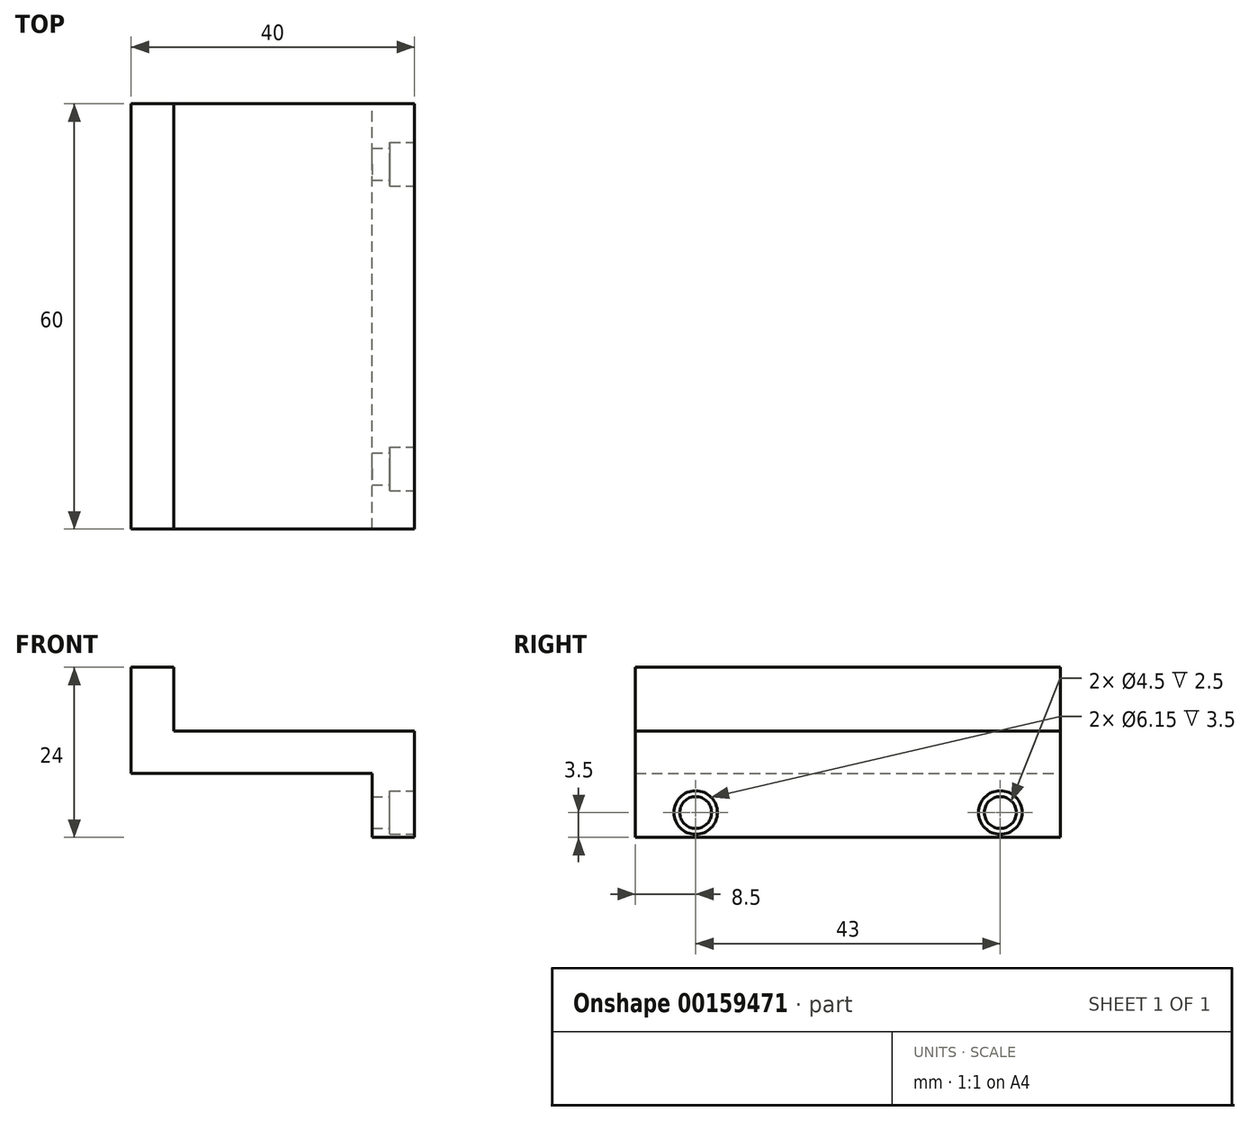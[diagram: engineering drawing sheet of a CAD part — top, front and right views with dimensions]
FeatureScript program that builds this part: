
annotation { "Feature Type Name" : "Feature", "Feature Type Description" : "" }
export const myFeature = defineFeature(function(context is Context, id is Id, definition is map)
    precondition{}
    {
        {
            var Q0;
            Q0=qCreatedBy(makeId("Top.planeOp"),FACE);
            var sketch = newSketch(context, id + "F0", { "sketchPlane" : qUnion([Q0])});
            skLineSegment(sketch, "E0.bottom", {"start": v(20, 30) * mm, "end": v(-20, 30) * mm});
            skLineSegment(sketch, "E0.top", {"start": v(20, -30) * mm, "end": v(-20, -30) * mm});
            skLineSegment(sketch, "E0.left", {"start": v(20, 30) * mm, "end": v(20, -30) * mm});
            skLineSegment(sketch, "E0.right", {"start": v(-20, 30) * mm, "end": v(-20, -30) * mm});
            skPoint(sketch, "E0.middle", {"position": v(0, 0) * mm});
            skSolve(sketch);
        }
        {
            var Q0;
            Q0=qSketchRegion(id+"F0",true);
            extrude(context, id + "F1", {"entities" : qUnion([Q0]), "depth" : 24 * mm});
        }
        {
            var Q0;
            Q0=makeQuery(id+"F1.opExtrude","CAP_FACE",FACE,{"disambiguationData":[OSD([sQuery(id+"F0.wireOp",EDGE,"E0.bottom"),sQuery(id+"F0.wireOp",EDGE,"E0.top"),sQuery(id+"F0.wireOp",EDGE,"E0.left"),sQuery(id+"F0.wireOp",EDGE,"E0.right")])],"isStart":false});
            var sketch = newSketch(context, id + "F2", { "sketchPlane" : qUnion([Q0])});
            skLineSegment(sketch, "E1.bottom", {"start": v(-14, 36.62) * mm, "end": v(51.94, 36.62) * mm});
            skLineSegment(sketch, "E1.top", {"start": v(-14, -36.62) * mm, "end": v(51.94, -36.62) * mm});
            skLineSegment(sketch, "E1.left", {"start": v(-14, 36.62) * mm, "end": v(-14, -36.62) * mm});
            skLineSegment(sketch, "E1.right", {"start": v(51.94, 36.62) * mm, "end": v(51.94, -36.62) * mm});
            skPoint(sketch, "E1.middle", {"position": v(18.97, 0) * mm});
            skSolve(sketch);
        }
        {
            var Q0;
            Q0=qSketchRegion(id+"F2",true);
            extrude(context, id + "F3", {"entities" : qUnion([Q0]), "operationType" : NewBodyOperationType.REMOVE, "oppositeDirection" : true, "depth" : 9 * mm});
        }
        {
            var Q0;
            Q0=makeQuery(id+"F1.opExtrude","CAP_FACE",FACE,{"disambiguationData":[OSD([sQuery(id+"F0.wireOp",EDGE,"E0.bottom"),sQuery(id+"F0.wireOp",EDGE,"E0.top"),sQuery(id+"F0.wireOp",EDGE,"E0.left"),sQuery(id+"F0.wireOp",EDGE,"E0.right")])],"isStart":true});
            var sketch = newSketch(context, id + "F4", { "sketchPlane" : qUnion([Q0])});
            skLineSegment(sketch, "E2.bottom", {"start": v(14, 34.98) * mm, "end": v(-52.14, 34.98) * mm});
            skLineSegment(sketch, "E2.top", {"start": v(14, -34.98) * mm, "end": v(-52.14, -34.98) * mm});
            skLineSegment(sketch, "E2.left", {"start": v(14, 34.98) * mm, "end": v(14, -34.98) * mm});
            skLineSegment(sketch, "E2.right", {"start": v(-52.14, 34.98) * mm, "end": v(-52.14, -34.98) * mm});
            skPoint(sketch, "E2.middle", {"position": v(-19.07, 0) * mm});
            skPoint(sketch, "E2.middle.positionSnap0", {"position": v(-20, 0) * mm});
            skPoint(sketch, "E2.centerSnap0", {"position": v(-20, 0) * mm});
            skSolve(sketch);
        }
        {
            var Q0;
            Q0=qSketchRegion(id+"F4",true);
            extrude(context, id + "F5", {"entities" : qUnion([Q0]), "operationType" : NewBodyOperationType.REMOVE, "oppositeDirection" : true, "depth" : 9 * mm});
        }
        {
            var Q0;
            Q0=makeQuery(id+"F1.opExtrude","SWEPT_FACE",FACE,{"disambiguationData":[OSD([sQuery(id+"F0.wireOp",EDGE,"E0.left")])]});
            var sketch = newSketch(context, id + "F6", { "sketchPlane" : qUnion([Q0])});
            skCircle(sketch, "E3", {"center": v(21.5, 3.5) * mm, "radius": 2.25 * mm});
            skCircle(sketch, "E4.MirrorC", {"center": v(-21.5, 3.5) * mm, "radius": 2.25 * mm});
            skSolve(sketch);
        }
        {
            var Q0;
            Q0=qSketchRegion(id+"F6",true);
            extrude(context, id + "F7", {"entities" : qUnion([Q0]), "operationType" : NewBodyOperationType.REMOVE, "oppositeDirection" : true, "depth" : 8 * mm});
        }
        {
            var Q0;
            Q0=makeQuery(id+"F1.opExtrude","SWEPT_FACE",FACE,{"disambiguationData":[OSD([sQuery(id+"F0.wireOp",EDGE,"E0.left")])]});
            var sketch = newSketch(context, id + "F8", { "sketchPlane" : qUnion([Q0])});
            skCircle(sketch, "E5", {"center": v(-21.5, 3.5) * mm, "radius": 3.07 * mm});
            skCircle(sketch, "E6.MirrorC", {"center": v(21.5, 3.5) * mm, "radius": 3.07 * mm});
            skSolve(sketch);
        }
        {
            var Q0;
            Q0=qSketchRegion(id+"F8",true);
            extrude(context, id + "F9", {"entities" : qUnion([Q0]), "operationType" : NewBodyOperationType.REMOVE, "oppositeDirection" : true, "depth" : 3.5 * mm});
        }
    });
